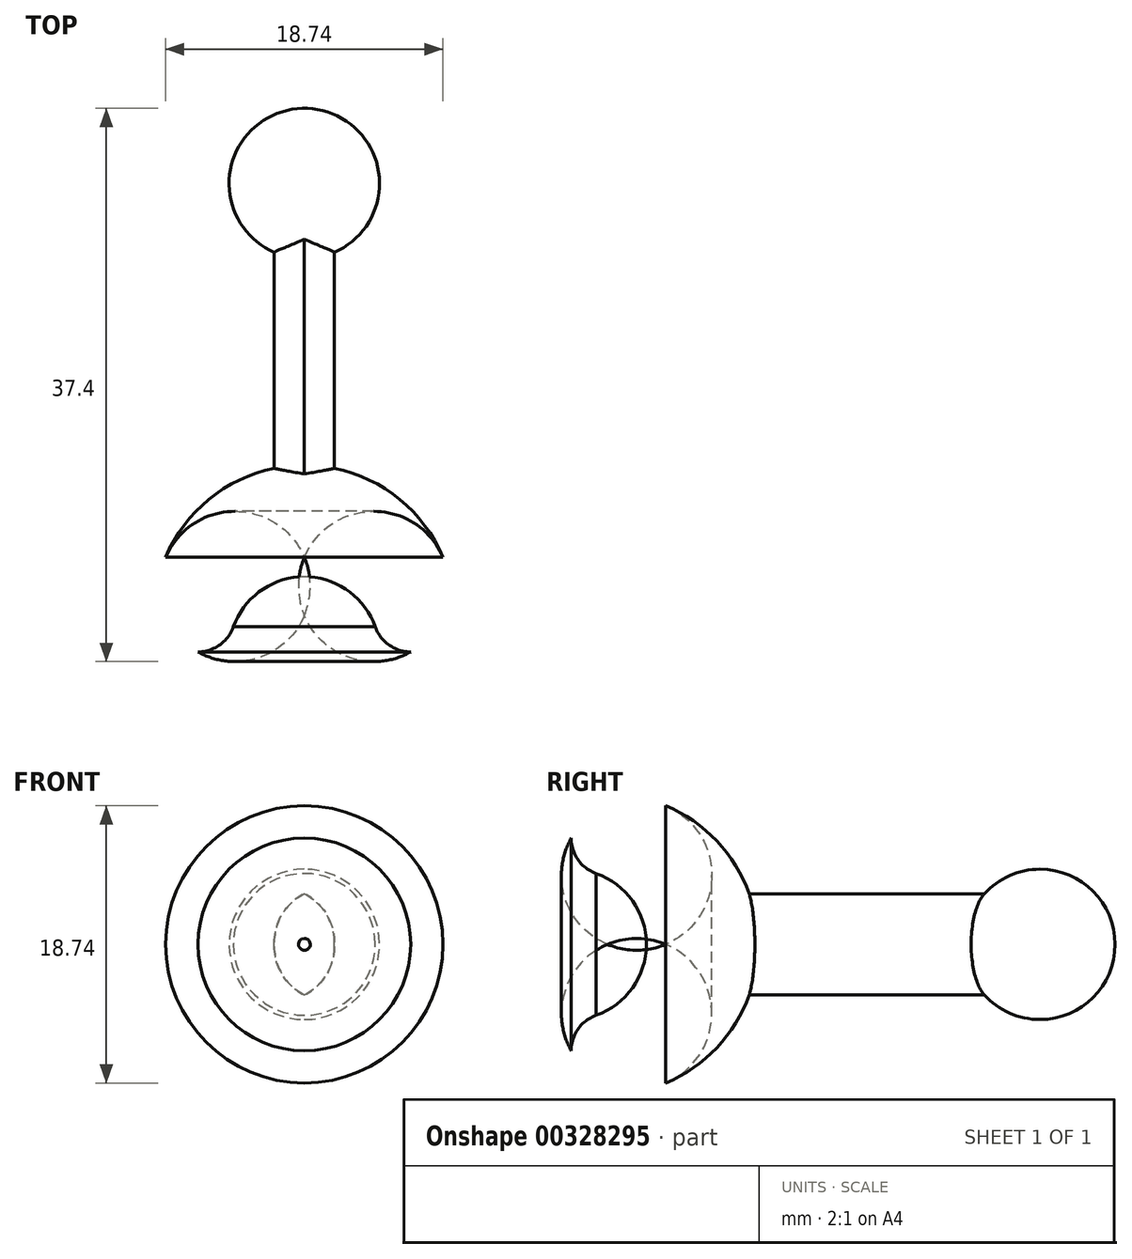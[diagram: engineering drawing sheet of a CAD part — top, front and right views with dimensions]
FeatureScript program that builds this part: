
annotation { "Feature Type Name" : "Feature", "Feature Type Description" : "" }
export const myFeature = defineFeature(function(context is Context, id is Id, definition is map)
    precondition{}
    {
        {
            var Q0;
            Q0=qCreatedBy(makeId("Front.planeOp"),FACE);
            var sketch = newSketch(context, id + "F0", { "sketchPlane" : qUnion([Q0])});
            skArc(sketch, "E0", {"start": v(0, 5.08) * mm, "mid": v(-5.08, 0) * mm, "end": v(0, -5.08) * mm});
            skLineSegment(sketch, "E1", {"start": v(0, 5.08) * mm, "end": v(0, -5.08) * mm});
            skSolve(sketch);
        }
        {
            var Q0;
            Q0 = qSketchRegion(id + "F0", true);
            var Q1;
            Q1=sQuery(id+"F0.wireOp",EDGE,"E1");
            revolve(context, id + "F1", {"entities" : qUnion([Q0]), "axis" : qUnion([Q1]), "revolveType" : RevolveType.FULL});
        }
        {
            var Q0;
            Q0=qCreatedBy(makeId("Front.planeOp"),FACE);
            var sketch = newSketch(context, id + "F2", { "sketchPlane" : qUnion([Q0])});
            skLineSegment(sketch, "E2.bottom", {"start": v(-2.03, 3.81) * mm, "end": v(2.03, 3.81) * mm});
            skLineSegment(sketch, "E2.top", {"start": v(-2.03, -3.81) * mm, "end": v(2.03, -3.81) * mm});
            skLineSegment(sketch, "E2.left", {"start": v(-2.03, 3.81) * mm, "end": v(-2.03, -3.81) * mm});
            skLineSegment(sketch, "E2.right", {"start": v(2.03, 3.81) * mm, "end": v(2.03, -3.81) * mm});
            skSolve(sketch);
        }
        {
            var Q0;
            Q0 = qSketchRegion(id + "F2", true);
            extrude(context, id + "F3", {"entities" : qUnion([Q0]), "operationType" : NewBodyOperationType.ADD, "depth" : 29.2 * mm});
        }
        {
            var Q0;
            Q0=makeQuery(id+"F3.opExtrude","CAP_FACE",FACE,{"disambiguationData":[OSD([sQuery(id+"F2.wireOp",EDGE,"E2.bottom"),sQuery(id+"F2.wireOp",EDGE,"E2.top"),sQuery(id+"F2.wireOp",EDGE,"E2.left"),sQuery(id+"F2.wireOp",EDGE,"E2.right")])],"isStart":false});
            var sketch = newSketch(context, id + "F4", { "sketchPlane" : qUnion([Q0])});
            skArc(sketch, "E3", {"start": v(0, 10.16) * mm, "mid": v(-10.16, 0) * mm, "end": v(0, -10.16) * mm});
            skPoint(sketch, "E3.startSnap0", {"position": v(0, 3.81) * mm});
            skLineSegment(sketch, "E4", {"start": v(0, 10.16) * mm, "end": v(0, -10.16) * mm});
            skSolve(sketch);
        }
        {
            var Q0;
            {var subQ5=makeQuery(id+"F3.opExtrude","CAP_EDGE",EDGE,{"disambiguationData":[OSD([sQuery(id+"F2.wireOp",EDGE,"E2.left")])],"isStart":false});Q0=makeQuery(id+"F4.imprint","IMPRINT",FACE,{"disambiguationData":[TD([[makeQuery(id+"F4.imprint","IMPRINT",EDGE,{"derivedFrom":subQ5}),1.0]])]});}
            var sketch = newSketch(context, id + "F5", { "sketchPlane" : qUnion([Q0])});
            skArc(sketch, "E5", {"start": v(0, 5.08) * mm, "mid": v(-5.08, 0) * mm, "end": v(0, -5.08) * mm});
            skLineSegment(sketch, "E6", {"start": v(0, 5.08) * mm, "end": v(0, -5.08) * mm});
            skSolve(sketch);
        }
        {
            var Q0;
            Q0 = qSketchRegion(id + "F5", true);
            var Q1;
            Q1=sQuery(id+"F5.wireOp",EDGE,"E6");
            revolve(context, id + "F6", {"operationType" : NewBodyOperationType.REMOVE, "entities" : qUnion([Q0]), "axis" : qUnion([Q1]), "revolveType" : RevolveType.FULL, "oppositeDirection" : true});
        }
        {
            var Q0;
            Q0 = qSketchRegion(id + "F4", true);
            var Q1;
            Q1=sQuery(id+"F4.wireOp",EDGE,"E4");
            revolve(context, id + "F7", {"operationType" : NewBodyOperationType.ADD, "entities" : qUnion([Q0]), "axis" : qUnion([Q1]), "revolveType" : RevolveType.FULL});
        }
        {
            var Q0;
            Q0=qCreatedBy(makeId("Right.planeOp"),FACE);
            var sketch = newSketch(context, id + "F8", { "sketchPlane" : qUnion([Q0])});
            skLineSegment(sketch, "E7.bottom", {"start": v(-31.66, 14.95) * mm, "end": v(-40.8, 14.95) * mm});
            skLineSegment(sketch, "E7.top", {"start": v(-31.66, -13.98) * mm, "end": v(-40.8, -13.98) * mm});
            skLineSegment(sketch, "E7.left", {"start": v(-31.66, 14.95) * mm, "end": v(-31.66, -13.98) * mm});
            skLineSegment(sketch, "E7.right", {"start": v(-40.8, 14.95) * mm, "end": v(-40.8, -13.98) * mm});
            skSolve(sketch);
        }
        {
            var Q0;
            Q0 = qSketchRegion(id + "F8", true);
            extrude(context, id + "F9", {"entities" : qUnion([Q0]), "operationType" : NewBodyOperationType.REMOVE, "endBound" : BoundingType.SYMMETRIC, "oppositeDirection" : true, "depth" : 25.4 * mm});
        }
        {
            var Q0;
            Q0=makeQuery(id+"F9.boolean.opBoolean","COPY",FACE,{"derivedFrom":makeQuery(id+"F9.opExtrude","SWEPT_FACE",FACE,{"disambiguationData":[OSD([sQuery(id+"F8.wireOp",EDGE,"E7.left")])]})});
            var sketch = newSketch(context, id + "F10", { "sketchPlane" : qUnion([Q0])});
            skArc(sketch, "E8", {"start": v(0, 5.08) * mm, "mid": v(-5.08, 0) * mm, "end": v(0, -5.08) * mm});
            skLineSegment(sketch, "E9", {"start": v(0, 5.08) * mm, "end": v(0, -5.08) * mm});
            skSolve(sketch);
        }
        {
            var Q0;
            Q0 = qSketchRegion(id + "F10", true);
            var Q1;
            Q1=sQuery(id+"F10.wireOp",EDGE,"E9");
            revolve(context, id + "F11", {"operationType" : NewBodyOperationType.REMOVE, "entities" : qUnion([Q0]), "axis" : qUnion([Q1]), "revolveType" : RevolveType.FULL, "oppositeDirection" : true});
        }
        {
            var Q0;
            Q0=makeQuery(id+"F11.boolean.opBoolean","INTERSECT",EDGE,{"derivedFrom":[makeQuery(id+"F9.boolean.opBoolean","COPY",FACE,{"derivedFrom":makeQuery(id+"F9.opExtrude","SWEPT_FACE",FACE,{"disambiguationData":[OSD([sQuery(id+"F8.wireOp",EDGE,"E7.left")])]})}),makeQuery(id+"F11.opRevolve","SWEPT_FACE",FACE,{"disambiguationData":[OSD([sQuery(id+"F10.wireOp",EDGE,"E8")])]})]});
            fillet(context, id + "F12", {"entities" : qUnion([Q0]), "radius" : 2.54 * mm, "tangentPropagation" : true, "allowEdgeOverflow" : false});
        }
        {
            var Q0;
            Q0=makeQuery(id+"F3.opExtrude","SWEPT_EDGE",EDGE,{"disambiguationData":[OSD([sQuery(id+"F2.wireOp",EDGE,"E2.bottom"),sQuery(id+"F2.wireOp",EDGE,"E2.left")])]});
            var Q1;
            Q1=makeQuery(id+"F3.opExtrude","SWEPT_EDGE",EDGE,{"disambiguationData":[OSD([sQuery(id+"F2.wireOp",EDGE,"E2.top"),sQuery(id+"F2.wireOp",EDGE,"E2.left")])]});
            var Q2;
            Q2=makeQuery(id+"F3.opExtrude","SWEPT_EDGE",EDGE,{"disambiguationData":[OSD([sQuery(id+"F2.wireOp",EDGE,"E2.top"),sQuery(id+"F2.wireOp",EDGE,"E2.right")])]});
            var Q3;
            Q3=makeQuery(id+"F3.opExtrude","SWEPT_EDGE",EDGE,{"disambiguationData":[OSD([sQuery(id+"F2.wireOp",EDGE,"E2.bottom"),sQuery(id+"F2.wireOp",EDGE,"E2.right")])]});
            fillet(context, id + "F13", {"entities" : qUnion([Q0, Q1, Q2, Q3]), "radius" : 3.68 * mm, "tangentPropagation" : true, "allowEdgeOverflow" : false});
        }
        {
            var Q0;
            Q0=makeQuery(id+"F9.boolean.opBoolean","INTERSECT",EDGE,{"derivedFrom":[makeQuery(id+"F7.opRevolve","SWEPT_FACE",FACE,{"disambiguationData":[OSD([sQuery(id+"F4.wireOp",EDGE,"E3")])]}),makeQuery(id+"F9.opExtrude","SWEPT_FACE",FACE,{"disambiguationData":[OSD([sQuery(id+"F8.wireOp",EDGE,"E7.left")])]})]});
            fillet(context, id + "F14", {"entities" : qUnion([Q0]), "radius" : 5.08 * mm, "tangentPropagation" : true, "allowEdgeOverflow" : false});
        }
    });
